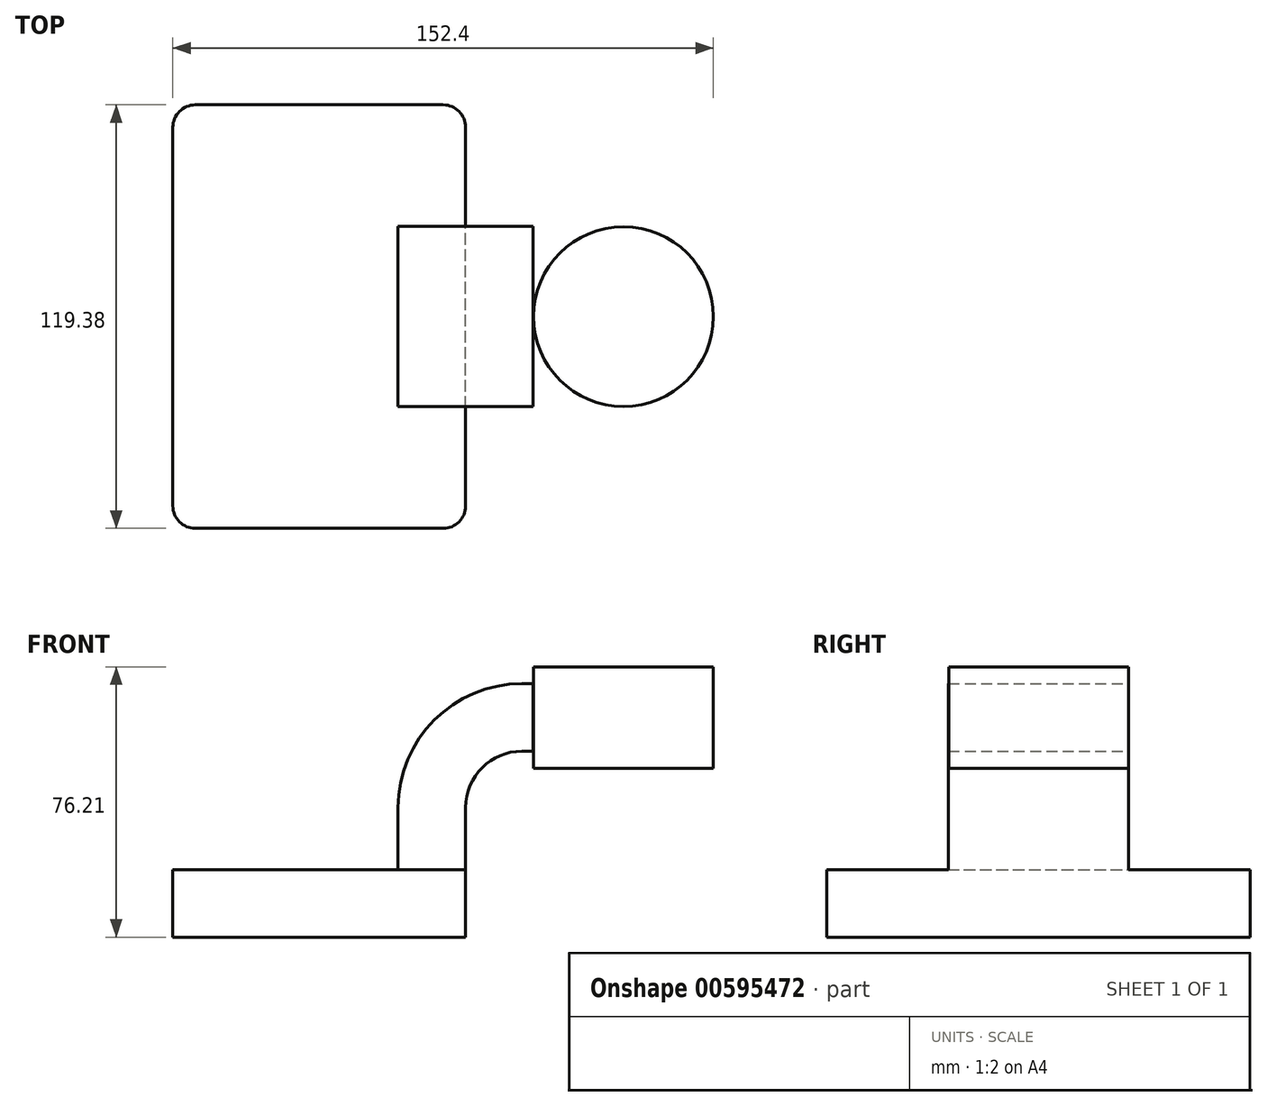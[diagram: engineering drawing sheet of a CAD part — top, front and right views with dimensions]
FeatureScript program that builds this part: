
annotation { "Feature Type Name" : "Feature", "Feature Type Description" : "" }
export const myFeature = defineFeature(function(context is Context, id is Id, definition is map)
    precondition{}
    {
        {
            var Q0;
            Q0=qCreatedBy(makeId("Front.planeOp"),FACE);
            var sketch = newSketch(context, id + "F0", { "sketchPlane" : qUnion([Q0])});
            skLineSegment(sketch, "E0.bottom", {"start": v(-41.28, 9.52) * mm, "end": v(41.28, 9.53) * mm});
            skLineSegment(sketch, "E0.top", {"start": v(-41.28, -9.53) * mm, "end": v(41.28, -9.53) * mm});
            skLineSegment(sketch, "E0.left", {"start": v(-41.28, 9.52) * mm, "end": v(-41.28, -9.53) * mm});
            skLineSegment(sketch, "E0.right", {"start": v(41.28, 9.53) * mm, "end": v(41.28, -9.52) * mm});
            skPoint(sketch, "E0.middle", {"position": v(0, 0) * mm});
            skLineSegment(sketch, "E1.bottom", {"start": v(111.12, 38.1) * mm, "end": v(60.32, 38.1) * mm});
            skLineSegment(sketch, "E1.top", {"start": v(111.12, 66.68) * mm, "end": v(60.32, 66.68) * mm});
            skLineSegment(sketch, "E1.left", {"start": v(111.12, 38.1) * mm, "end": v(111.12, 66.68) * mm});
            skLineSegment(sketch, "E1.right", {"start": v(60.32, 38.1) * mm, "end": v(60.32, 66.68) * mm});
            skPoint(sketch, "E1.middle", {"position": v(85.72, 52.39) * mm});
            skLineSegment(sketch, "E2", {"start": v(41.27, 9.53) * mm, "end": v(41.27, 27) * mm});
            skArc(sketch, "E3", {"start": v(41.27, 27) * mm, "mid": v(45.92, 38.23) * mm, "end": v(57.15, 42.88) * mm});
            skLineSegment(sketch, "E4", {"start": v(57.15, 42.88) * mm, "end": v(85.77, 42.88) * mm});
            skLineSegment(sketch, "E5.0", {"start": v(57.15, 61.93) * mm, "end": v(85.77, 61.93) * mm});
            skArc(sketch, "E5.1", {"start": v(22.22, 27) * mm, "mid": v(32.45, 51.7) * mm, "end": v(57.15, 61.93) * mm});
            skLineSegment(sketch, "E5.2", {"start": v(22.22, 9.53) * mm, "end": v(22.22, 27) * mm});
            skLineSegment(sketch, "E6", {"start": v(85.77, 46.58) * mm, "end": v(85.77, 61.93) * mm});
            skFitSpline(sketch, "E7", {"points": [v(-41.28, 9.52) * mm, v(57.15, 61.93) * mm], "startDerivative": vector(0.43, 78.73) * mm, "endDerivative": vector(98.44, -0.32) * mm});
            skLineSegment(sketch, "E8", {"start": v(85.77, 46.58) * mm, "end": v(85.77, 66.68) * mm});
            skLineSegment(sketch, "E9", {"start": v(85.77, 38.1) * mm, "end": v(85.77, 66.68) * mm});
            skPoint(sketch, "E9.startSnap0", {"position": v(85.72, 38.1) * mm});
            skSolve(sketch);
        }
        {
            var Q0;
            Q0=makeQuery(id+"F0.imprint","IMPRINT",FACE,{"disambiguationData":[TD([[makeQuery(id+"F0.imprint","IMPRINT",EDGE,{"derivedFrom":sQuery(id+"F0.wireOp",EDGE,"E0.top")}),1.0]])]});
            extrude(context, id + "F1", {"entities" : qUnion([Q0]), "endBound" : BoundingType.SYMMETRIC, "depth" : 119.38 * mm, "offsetDistance" : 25.4 * mm});
        }
        {
            var Q0;
            {var subQ1=sQuery(id+"F0.wireOp",EDGE,"E2");Q0=makeQuery(id+"F0.imprint","IMPRINT",FACE,{"disambiguationData":[TD([[makeQuery(id+"F0.imprint","IMPRINT",EDGE,{"derivedFrom":subQ1}),1.0]])]});}
            var Q1;
            {var subQ0=sQuery(id+"F0.wireOp",EDGE,"E9");var subQ3=makeQuery(id+"F0.imprint","IMPRINT",VERTEX,{"derivedFrom":subQ0});Q1=makeQuery(id+"F0.imprint","IMPRINT",FACE,{"disambiguationData":[TD([[makeQuery(id+"F0.imprint","IMPRINT",EDGE,{"disambiguationData":[TD([[subQ3,1.0]])],"derivedFrom":subQ0}),1.0]])]});}
            extrude(context, id + "F2", {"entities" : qUnion([Q0, Q1]), "operationType" : NewBodyOperationType.ADD, "endBound" : BoundingType.SYMMETRIC, "depth" : 50.8 * mm, "offsetDistance" : 25.4 * mm});
        }
        {
            var Q0;
            {var subQ1=sQuery(id+"F0.wireOp",EDGE,"E2");Q0=makeQuery(id+"F0.imprint","IMPRINT",FACE,{"disambiguationData":[TD([[makeQuery(id+"F0.imprint","IMPRINT",EDGE,{"derivedFrom":subQ1}),1.0]])]});}
            var Q1;
            {var subQ0=sQuery(id+"F0.wireOp",EDGE,"E9");var subQ3=makeQuery(id+"F0.imprint","IMPRINT",VERTEX,{"derivedFrom":subQ0});Q1=makeQuery(id+"F0.imprint","IMPRINT",FACE,{"disambiguationData":[TD([[makeQuery(id+"F0.imprint","IMPRINT",EDGE,{"disambiguationData":[TD([[subQ3,1.0]])],"derivedFrom":subQ0}),1.0]])]});}
            extrude(context, id + "F3", {"entities" : qUnion([Q0, Q1]), "operationType" : NewBodyOperationType.ADD, "depth" : 25.4 * mm, "offsetDistance" : 25.4 * mm});
        }
        {
            var Q0;
            Q0=makeQuery(id+"F0.imprint","IMPRINT",FACE,{"disambiguationData":[TD([[makeQuery(id+"F0.imprint","IMPRINT",EDGE,{"derivedFrom":sQuery(id+"F0.wireOp",EDGE,"E5.1")}),1.0]])]});
            extrude(context, id + "F4", {"entities" : qUnion([Q0]), "operationType" : NewBodyOperationType.ADD, "endBound" : BoundingType.SYMMETRIC, "depth" : 15.88 * mm, "offsetDistance" : 25.4 * mm});
        }
        {
            var Q0;
            {var subQ0=sQuery(id+"F0.wireOp",EDGE,"E1.left");Q0=makeQuery(id+"F0.imprint","IMPRINT",FACE,{"disambiguationData":[TD([[makeQuery(id+"F0.imprint","IMPRINT",EDGE,{"derivedFrom":subQ0}),1.0]])]});}
            var Q1;
            Q1=sQuery(id+"F0.wireOp",EDGE,"E8");
            revolve(context, id + "F5", {"operationType" : NewBodyOperationType.ADD, "entities" : qUnion([Q0]), "axis" : qUnion([Q1]), "revolveType" : RevolveType.FULL});
        }
        {
            var Q0;
            Q0=makeQuery(id+"F1.opExtrude","CAP_EDGE",EDGE,{"disambiguationData":[OSD([sQuery(id+"F0.wireOp",EDGE,"E0.right")])],"isStart":false});
            var Q1;
            Q1=makeQuery(id+"F1.opExtrude","CAP_EDGE",EDGE,{"disambiguationData":[OSD([sQuery(id+"F0.wireOp",EDGE,"E0.left")])],"isStart":false});
            var Q2;
            Q2=makeQuery(id+"F1.opExtrude","CAP_EDGE",EDGE,{"disambiguationData":[OSD([sQuery(id+"F0.wireOp",EDGE,"E0.left")])],"isStart":true});
            var Q3;
            Q3=makeQuery(id+"F1.opExtrude","CAP_EDGE",EDGE,{"disambiguationData":[OSD([sQuery(id+"F0.wireOp",EDGE,"E0.right")])],"isStart":true});
            fillet(context, id + "F6", {"entities" : qUnion([Q0, Q1, Q2, Q3]), "radius" : 6.35 * mm, "tangentPropagation" : true, "allowEdgeOverflow" : false});
        }
    });
